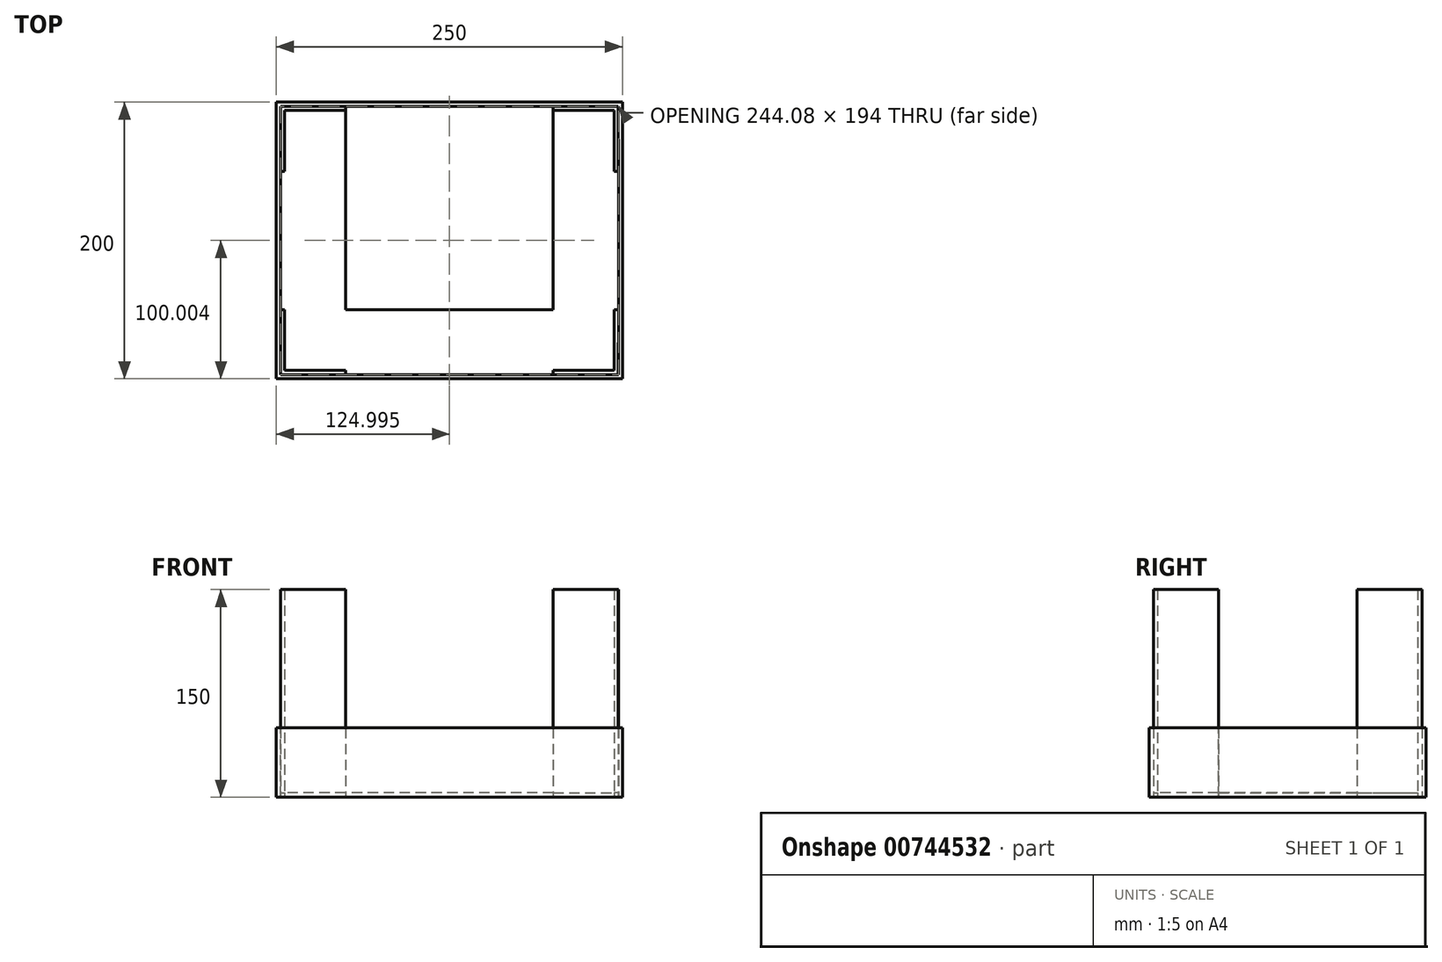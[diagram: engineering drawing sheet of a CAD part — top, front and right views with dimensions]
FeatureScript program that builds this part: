
annotation { "Feature Type Name" : "Feature", "Feature Type Description" : "" }
export const myFeature = defineFeature(function(context is Context, id is Id, definition is map)
    precondition{}
    {
        {
            var Q0;
            Q0=qCreatedBy(makeId("Top.planeOp"),FACE);
            var sketch = newSketch(context, id + "F0", { "sketchPlane" : qUnion([Q0])});
            skLineSegment(sketch, "E0.bottom", {"start": v(-136.64, 96.22) * mm, "end": v(-89.64, 96.22) * mm});
            skLineSegment(sketch, "E0.top", {"start": v(-139.64, -103.78) * mm, "end": v(110.36, -103.78) * mm});
            skLineSegment(sketch, "E0.left", {"start": v(-139.64, 96.22) * mm, "end": v(-139.64, -103.78) * mm});
            skLineSegment(sketch, "E0.right", {"start": v(110.36, 96.22) * mm, "end": v(110.36, -103.78) * mm});
            skLineSegment(sketch, "E1", {"start": v(-89.64, 46.22) * mm, "end": v(-89.64, -53.78) * mm});
            skLineSegment(sketch, "E2", {"start": v(-89.64, 46.22) * mm, "end": v(60.36, 46.22) * mm});
            skLineSegment(sketch, "E3", {"start": v(110.36, 96.22) * mm, "end": v(60.36, 96.22) * mm});
            skLineSegment(sketch, "E4", {"start": v(60.36, 46.22) * mm, "end": v(60.36, -53.78) * mm});
            skLineSegment(sketch, "E5", {"start": v(110.36, -103.78) * mm, "end": v(110.36, -53.78) * mm});
            skLineSegment(sketch, "E6", {"start": v(60.36, -53.78) * mm, "end": v(-89.64, -53.78) * mm});
            skPoint(sketch, "E7.end.orphan", {"position": v(-89.64, 96.22) * mm});
            skLineSegment(sketch, "E8", {"start": v(-89.64, 93.22) * mm, "end": v(-136.65, 93.22) * mm});
            skLineSegment(sketch, "E9", {"start": v(-139.64, 96.22) * mm, "end": v(-139.64, 46.22) * mm});
            skLineSegment(sketch, "E10", {"start": v(-136.69, 46.22) * mm, "end": v(-136.65, 93.22) * mm});
            skLineSegment(sketch, "E11", {"start": v(-139.64, 96.22) * mm, "end": v(-14.64, 96.22) * mm});
            skLineSegment(sketch, "E12.MirrorCS", {"start": v(60.36, 93.22) * mm, "end": v(107.36, 93.22) * mm});
            skLineSegment(sketch, "E13.MirrorCS", {"start": v(107.4, 46.22) * mm, "end": v(107.36, 93.22) * mm});
            skLineSegment(sketch, "E14", {"start": v(-139.64, 96.22) * mm, "end": v(-139.64, -3.78) * mm});
            skLineSegment(sketch, "E15.MirrorCS", {"start": v(-136.69, -53.78) * mm, "end": v(-136.65, -100.78) * mm});
            skLineSegment(sketch, "E16.MirrorCS", {"start": v(-89.64, -100.78) * mm, "end": v(-136.65, -100.78) * mm});
            skLineSegment(sketch, "E17.MirrorCS", {"start": v(107.4, -53.78) * mm, "end": v(107.36, -100.78) * mm});
            skLineSegment(sketch, "E18.MirrorCS", {"start": v(60.36, -100.78) * mm, "end": v(107.36, -100.78) * mm});
            skLineSegment(sketch, "E19", {"start": v(-136.69, 46.22) * mm, "end": v(-136.69, -53.78) * mm});
            skLineSegment(sketch, "E20", {"start": v(-89.64, 93.22) * mm, "end": v(60.36, 93.22) * mm});
            skLineSegment(sketch, "E21", {"start": v(107.4, 46.22) * mm, "end": v(107.4, -53.78) * mm});
            skLineSegment(sketch, "E22", {"start": v(60.36, -100.78) * mm, "end": v(-89.64, -100.78) * mm});
            skLineSegment(sketch, "E23", {"start": v(-89.64, 93.22) * mm, "end": v(-89.64, 90.22) * mm});
            skLineSegment(sketch, "E24", {"start": v(-89.64, 90.22) * mm, "end": v(-133.69, 90.22) * mm});
            skLineSegment(sketch, "E25", {"start": v(-136.69, 46.22) * mm, "end": v(-133.69, 46.22) * mm});
            skLineSegment(sketch, "E26", {"start": v(-133.69, 46.22) * mm, "end": v(-133.69, 90.22) * mm});
            skLineSegment(sketch, "E27.MirrorCS", {"start": v(60.36, 93.22) * mm, "end": v(60.36, 90.22) * mm});
            skLineSegment(sketch, "E28.MirrorCS", {"start": v(60.36, 90.22) * mm, "end": v(104.4, 90.22) * mm});
            skLineSegment(sketch, "E29.MirrorCS", {"start": v(104.4, 46.22) * mm, "end": v(104.4, 90.22) * mm});
            skLineSegment(sketch, "E30.MirrorCS", {"start": v(107.4, 46.22) * mm, "end": v(104.4, 46.22) * mm});
            skLineSegment(sketch, "E31.MirrorCS", {"start": v(-136.69, -53.78) * mm, "end": v(-133.69, -53.77) * mm});
            skLineSegment(sketch, "E32.MirrorCS", {"start": v(-133.69, -53.77) * mm, "end": v(-133.69, -97.78) * mm});
            skLineSegment(sketch, "E33.MirrorCS", {"start": v(-89.64, -97.78) * mm, "end": v(-133.69, -97.78) * mm});
            skLineSegment(sketch, "E34.MirrorCS", {"start": v(-89.64, -100.78) * mm, "end": v(-89.64, -97.78) * mm});
            skLineSegment(sketch, "E35.MirrorCS", {"start": v(104.4, -53.77) * mm, "end": v(104.4, -97.78) * mm});
            skLineSegment(sketch, "E36.MirrorCS", {"start": v(60.36, -97.78) * mm, "end": v(104.4, -97.78) * mm});
            skLineSegment(sketch, "E37.MirrorCS", {"start": v(60.36, -100.78) * mm, "end": v(60.36, -97.78) * mm});
            skLineSegment(sketch, "E38.MirrorCS", {"start": v(107.4, -53.78) * mm, "end": v(104.4, -53.77) * mm});
            skLineSegment(sketch, "E39.bottom", {"start": v(-136.65, -100.78) * mm, "end": v(-89.64, -100.78) * mm});
            skLineSegment(sketch, "E39.top", {"start": v(-136.65, 93.22) * mm, "end": v(-89.64, 93.22) * mm});
            skLineSegment(sketch, "E39.left", {"start": v(-136.65, -100.78) * mm, "end": v(-136.65, 93.22) * mm});
            skLineSegment(sketch, "E39.right", {"start": v(-89.64, -100.78) * mm, "end": v(-89.64, 93.22) * mm});
            skLineSegment(sketch, "E40.bottom", {"start": v(-89.64, -100.78) * mm, "end": v(107.4, -100.78) * mm});
            skLineSegment(sketch, "E40.top", {"start": v(-89.64, -53.78) * mm, "end": v(107.4, -53.78) * mm});
            skLineSegment(sketch, "E40.left", {"start": v(-89.64, -100.78) * mm, "end": v(-89.64, -53.78) * mm});
            skLineSegment(sketch, "E40.right", {"start": v(107.4, -100.78) * mm, "end": v(107.4, -53.78) * mm});
            skLineSegment(sketch, "E41.bottom", {"start": v(60.36, -53.78) * mm, "end": v(107.36, -53.78) * mm});
            skLineSegment(sketch, "E41.left", {"start": v(60.36, -53.78) * mm, "end": v(60.36, 93.22) * mm});
            skLineSegment(sketch, "E41.right", {"start": v(107.36, 46.22) * mm, "end": v(107.36, 93.22) * mm});
            skLineSegment(sketch, "E42.bottom", {"start": v(60.36, 93.22) * mm, "end": v(-89.64, 93.22) * mm});
            skLineSegment(sketch, "E42.top", {"start": v(60.36, 46.22) * mm, "end": v(-89.64, 46.22) * mm});
            skLineSegment(sketch, "E42.left", {"start": v(60.36, 93.22) * mm, "end": v(60.36, 46.22) * mm});
            skLineSegment(sketch, "E42.right", {"start": v(-89.64, 93.22) * mm, "end": v(-89.64, 46.22) * mm});
            skLineSegment(sketch, "E43.top", {"start": v(-136.65, -53.78) * mm, "end": v(-89.64, -53.78) * mm});
            skLineSegment(sketch, "E43.left", {"start": v(-136.65, -100.78) * mm, "end": v(-136.65, -53.78) * mm});
            skLineSegment(sketch, "E44.trimOffspring", {"start": v(-14.64, 96.22) * mm, "end": v(110.36, 96.22) * mm});
            skSolve(sketch);
        }
        {
            var Q0;
            {var subQ5=sQuery(id+"F0.wireOp",EDGE,"E24");Q0=makeQuery(id+"F0.imprint","IMPRINT",FACE,{"disambiguationData":[TD([[makeQuery(id+"F0.imprint","IMPRINT",EDGE,{"derivedFrom":subQ5}),-1.0]])]});}
            extrude(context, id + "F1", {"entities" : qUnion([Q0]), "depth" : 150 * mm, "offsetDistance" : 25 * mm});
        }
        {
            var Q0;
            {var subQ4=sQuery(id+"F0.wireOp",EDGE,"E28.MirrorCS");Q0=makeQuery(id+"F0.imprint","IMPRINT",FACE,{"disambiguationData":[TD([[makeQuery(id+"F0.imprint","IMPRINT",EDGE,{"derivedFrom":subQ4}),1.0]])]});}
            var Q1;
            {var subQ3=sQuery(id+"F0.wireOp",EDGE,"E17.MirrorCS");Q1=makeQuery(id+"F0.imprint","IMPRINT",FACE,{"disambiguationData":[TD([[makeQuery(id+"F0.imprint","IMPRINT",EDGE,{"derivedFrom":subQ3}),-1.0]])]});}
            var Q2;
            {var subQ5=sQuery(id+"F0.wireOp",EDGE,"E33.MirrorCS");Q2=makeQuery(id+"F0.imprint","IMPRINT",FACE,{"disambiguationData":[TD([[makeQuery(id+"F0.imprint","IMPRINT",EDGE,{"derivedFrom":subQ5}),1.0]])]});}
            extrude(context, id + "F2", {"entities" : qUnion([Q0, Q1, Q2]), "depth" : 150 * mm, "offsetDistance" : 25 * mm});
        }
        {
            var Q0;
            Q0=makeQuery(id+"F0.imprint","IMPRINT",FACE,{"disambiguationData":[TD([[makeQuery(id+"F0.imprint","IMPRINT",EDGE,{"derivedFrom":sQuery(id+"F0.wireOp",EDGE,"E0.top")}),1.0]])]});
            extrude(context, id + "F3", {"entities" : qUnion([Q0]), "depth" : 50 * mm, "offsetDistance" : 25 * mm});
        }
        {
            var Q0;
            {var subQ0=sQuery(id+"F0.wireOp",EDGE,"E33.MirrorCS");Q0=makeQuery(id+"F0.imprint","IMPRINT",FACE,{"disambiguationData":[TD([[makeQuery(id+"F0.imprint","IMPRINT",EDGE,{"derivedFrom":subQ0}),-1.0]])]});}
            var Q1;
            {var subQ9=sQuery(id+"F0.wireOp",EDGE,"E24");Q1=makeQuery(id+"F0.imprint","IMPRINT",FACE,{"disambiguationData":[TD([[makeQuery(id+"F0.imprint","IMPRINT",EDGE,{"derivedFrom":subQ9}),1.0]])]});}
            var Q2;
            {var subQ7=sQuery(id+"F0.wireOp",EDGE,"E36.MirrorCS");Q2=makeQuery(id+"F0.imprint","IMPRINT",FACE,{"disambiguationData":[TD([[makeQuery(id+"F0.imprint","IMPRINT",EDGE,{"derivedFrom":subQ7}),1.0]])]});}
            var Q3;
            {var subQ10=sQuery(id+"F0.wireOp",EDGE,"E21");Q3=makeQuery(id+"F0.imprint","IMPRINT",FACE,{"disambiguationData":[TD([[makeQuery(id+"F0.imprint","IMPRINT",EDGE,{"derivedFrom":subQ10}),-1.0]])]});}
            var Q4;
            {var subQ3=sQuery(id+"F0.wireOp",EDGE,"E42.bottom");Q4=makeQuery(id+"F0.imprint","IMPRINT",FACE,{"disambiguationData":[TD([[makeQuery(id+"F0.imprint","IMPRINT",EDGE,{"derivedFrom":subQ3}),1.0]])]});}
            extrude(context, id + "F4", {"entities" : qUnion([Q0, Q1, Q2, Q3, Q4]), "depth" : 3 * mm, "offsetDistance" : 25 * mm});
        }
    });
